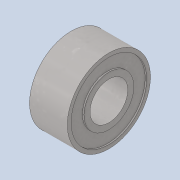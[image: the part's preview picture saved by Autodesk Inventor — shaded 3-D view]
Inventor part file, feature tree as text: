
AUTODESK INVENTOR PART (.ipt)
format: ipt  version: 2020.4 (Build 244396000, 396)  size: 136,704 bytes
history: native  units: mm
features: other x1, revolve x1, sketch x1
ambient origin geometry x8: Origin, YZ Plane, XZ Plane, XY Plane, X Axis, Y Axis, Z Axis, Center Point
bodies: Volumenkörper1 (feature_tree)
feature tree (3):
  other  "Kugellager 685-ZZ-C3"
  revolve  "Umdrehung1"
  sketch  "Skizze1"  dims[d0=5.0mm d1=11.0mm d2=5.0mm d3=0.2mm d4=0.8mm d5=0.5mm d6=90.0deg]
